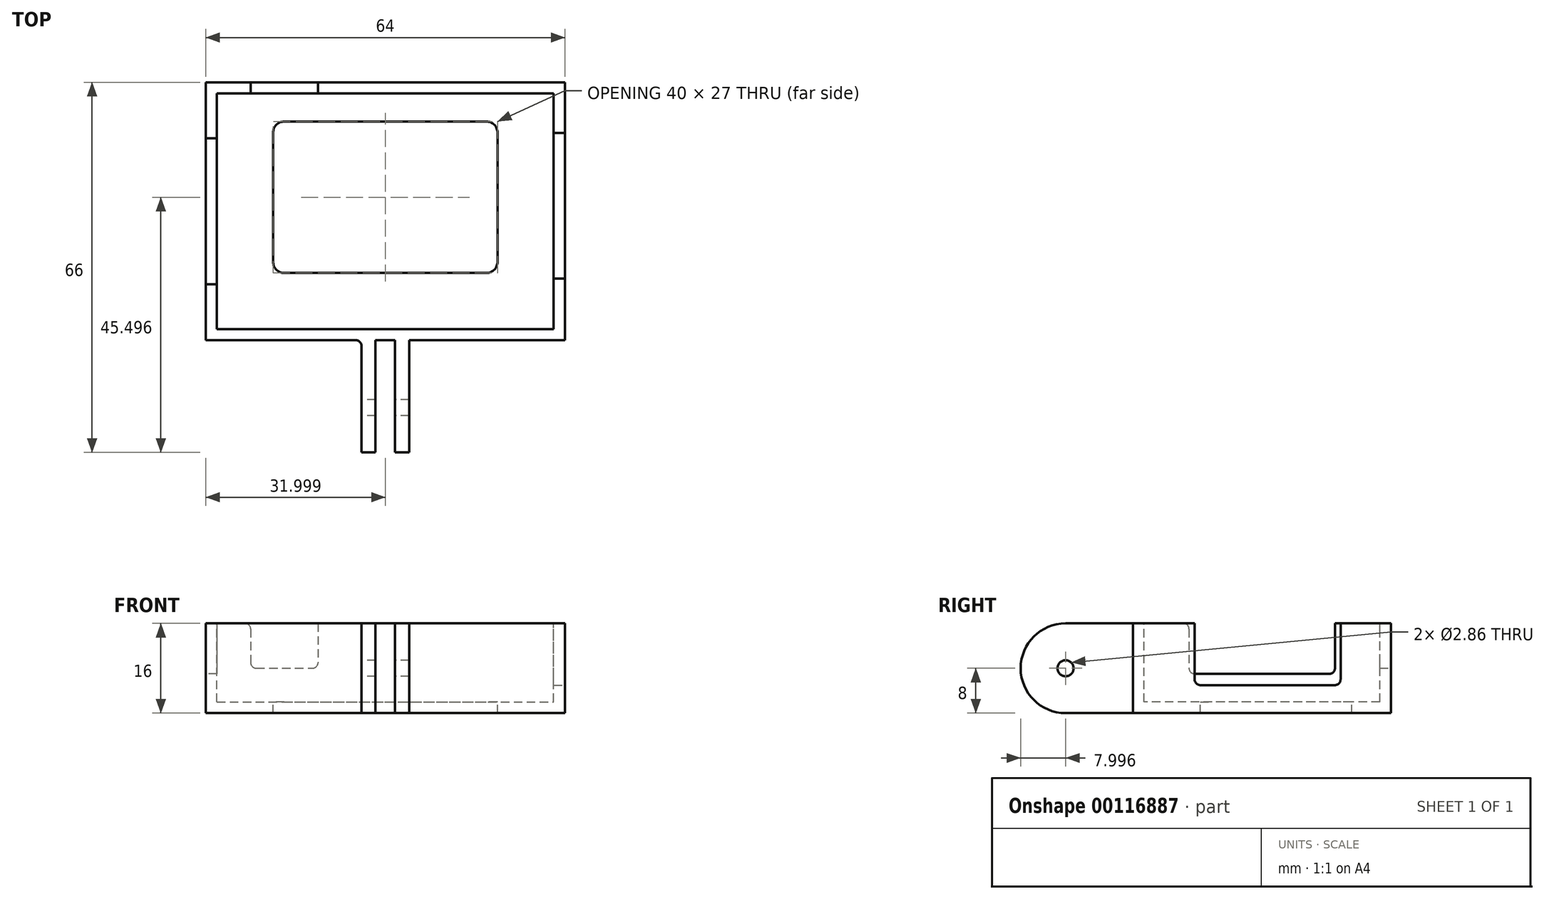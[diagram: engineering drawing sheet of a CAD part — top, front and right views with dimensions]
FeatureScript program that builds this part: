
annotation { "Feature Type Name" : "Feature", "Feature Type Description" : "" }
export const myFeature = defineFeature(function(context is Context, id is Id, definition is map)
    precondition{}
    {
        {
            var Q0;
            Q0=qCreatedBy(makeId("Top.planeOp"),FACE);
            var sketch = newSketch(context, id + "F0", { "sketchPlane" : qUnion([Q0])});
            skLineSegment(sketch, "E0.bottom", {"start": v(-24.87, 23.52) * mm, "end": v(39.13, 23.52) * mm});
            skLineSegment(sketch, "E0.top", {"start": v(-24.87, -22.48) * mm, "end": v(39.13, -22.48) * mm});
            skLineSegment(sketch, "E0.left", {"start": v(-24.87, 23.52) * mm, "end": v(-24.87, -22.48) * mm});
            skLineSegment(sketch, "E0.right", {"start": v(39.13, 23.52) * mm, "end": v(39.13, -22.48) * mm});
            skSolve(sketch);
        }
        {
            var Q0;
            Q0=makeQuery(id+"F0.imprint","IMPRINT",FACE,{"disambiguationData":[TD([[makeQuery(id+"F0.imprint","IMPRINT",EDGE,{"derivedFrom":sQuery(id+"F0.wireOp",EDGE,"E0.bottom")}),-1.0]])]});
            extrude(context, id + "F1", {"entities" : qUnion([Q0]), "depth" : 16 * mm});
        }
        {
            var Q0;
            Q0=makeQuery(id+"F1.opExtrude","CAP_FACE",FACE,{"disambiguationData":[OSD([sQuery(id+"F0.wireOp",EDGE,"E0.bottom"),sQuery(id+"F0.wireOp",EDGE,"E0.top"),sQuery(id+"F0.wireOp",EDGE,"E0.left"),sQuery(id+"F0.wireOp",EDGE,"E0.right")])],"isStart":false});
            var sketch = newSketch(context, id + "F2", { "sketchPlane" : qUnion([Q0])});
            skLineSegment(sketch, "E1.bottom", {"start": v(-22.87, 21.52) * mm, "end": v(37.13, 21.52) * mm});
            skLineSegment(sketch, "E1.top", {"start": v(-22.87, -20.48) * mm, "end": v(37.13, -20.48) * mm});
            skLineSegment(sketch, "E1.left", {"start": v(-22.87, 21.52) * mm, "end": v(-22.87, -20.48) * mm});
            skLineSegment(sketch, "E1.right", {"start": v(37.13, 21.52) * mm, "end": v(37.13, -20.48) * mm});
            skSolve(sketch);
        }
        {
            var Q0;
            Q0=makeQuery(id+"F2.imprint","IMPRINT",FACE,{"disambiguationData":[TD([[makeQuery(id+"F2.imprint","IMPRINT",EDGE,{"derivedFrom":sQuery(id+"F2.wireOp",EDGE,"E1.bottom")}),-1.0]])]});
            extrude(context, id + "F3", {"entities" : qUnion([Q0]), "operationType" : NewBodyOperationType.REMOVE, "oppositeDirection" : true, "depth" : 14 * mm});
        }
        {
            var Q0;
            Q0=makeQuery(id+"F3.boolean.opBoolean","COPY",FACE,{"derivedFrom":makeQuery(id+"F3.opExtrude","CAP_FACE",FACE,{"disambiguationData":[OSD([sQuery(id+"F2.wireOp",EDGE,"E1.bottom"),sQuery(id+"F2.wireOp",EDGE,"E1.top"),sQuery(id+"F2.wireOp",EDGE,"E1.left"),sQuery(id+"F2.wireOp",EDGE,"E1.right")])],"isStart":false})});
            var sketch = newSketch(context, id + "F4", { "sketchPlane" : qUnion([Q0])});
            skLineSegment(sketch, "E2.bottom", {"start": v(-12.87, 16.52) * mm, "end": v(27.13, 16.52) * mm});
            skLineSegment(sketch, "E2.top", {"start": v(-12.87, -10.48) * mm, "end": v(27.13, -10.48) * mm});
            skLineSegment(sketch, "E2.left", {"start": v(-12.87, 16.52) * mm, "end": v(-12.87, -10.48) * mm});
            skLineSegment(sketch, "E2.right", {"start": v(27.13, 16.52) * mm, "end": v(27.13, -10.48) * mm});
            skSolve(sketch);
        }
        {
            var Q0;
            Q0=makeQuery(id+"F4.imprint","IMPRINT",FACE,{"disambiguationData":[TD([[makeQuery(id+"F4.imprint","IMPRINT",EDGE,{"derivedFrom":sQuery(id+"F4.wireOp",EDGE,"E2.bottom")}),-1.0]])]});
            extrude(context, id + "F5", {"entities" : qUnion([Q0]), "operationType" : NewBodyOperationType.REMOVE, "oppositeDirection" : true, "depth" : 25 * mm});
        }
        {
            var Q0;
            Q0=makeQuery(id+"F5.boolean.opBoolean","COPY",EDGE,{"derivedFrom":makeQuery(id+"F5.opExtrude","SWEPT_EDGE",EDGE,{"disambiguationData":[OSD([sQuery(id+"F4.wireOp",EDGE,"E2.bottom"),sQuery(id+"F4.wireOp",EDGE,"E2.left")])]})});
            var Q1;
            Q1=makeQuery(id+"F5.boolean.opBoolean","COPY",EDGE,{"derivedFrom":makeQuery(id+"F5.opExtrude","SWEPT_EDGE",EDGE,{"disambiguationData":[OSD([sQuery(id+"F4.wireOp",EDGE,"E2.top"),sQuery(id+"F4.wireOp",EDGE,"E2.left")])]})});
            var Q2;
            Q2=makeQuery(id+"F5.boolean.opBoolean","COPY",EDGE,{"derivedFrom":makeQuery(id+"F5.opExtrude","SWEPT_EDGE",EDGE,{"disambiguationData":[OSD([sQuery(id+"F4.wireOp",EDGE,"E2.top"),sQuery(id+"F4.wireOp",EDGE,"E2.right")])]})});
            var Q3;
            Q3=makeQuery(id+"F5.boolean.opBoolean","COPY",EDGE,{"derivedFrom":makeQuery(id+"F5.opExtrude","SWEPT_EDGE",EDGE,{"disambiguationData":[OSD([sQuery(id+"F4.wireOp",EDGE,"E2.bottom"),sQuery(id+"F4.wireOp",EDGE,"E2.right")])]})});
            fillet(context, id + "F6", {"entities" : qUnion([Q0, Q1, Q2, Q3]), "radius" : 2 * mm, "tangentPropagation" : true, "allowEdgeOverflow" : false});
        }
        {
            var Q0;
            Q0=makeQuery(id+"F1.opExtrude","SWEPT_FACE",FACE,{"disambiguationData":[OSD([sQuery(id+"F0.wireOp",EDGE,"E0.top")])]});
            var sketch = newSketch(context, id + "F7", { "sketchPlane" : qUnion([Q0])});
            skLineSegment(sketch, "E3.bottom", {"start": v(2.88, 16) * mm, "end": v(5.38, 16) * mm});
            skLineSegment(sketch, "E3.top", {"start": v(2.88, 0) * mm, "end": v(5.38, 0) * mm});
            skLineSegment(sketch, "E3.left", {"start": v(2.88, 16) * mm, "end": v(2.88, 0) * mm});
            skLineSegment(sketch, "E3.right", {"start": v(5.38, 16) * mm, "end": v(5.38, 0) * mm});
            skLineSegment(sketch, "E4.1.0.0", {"start": v(8.88, 16) * mm, "end": v(8.88, 0) * mm});
            skLineSegment(sketch, "E4.1.0.1", {"start": v(11.38, 16) * mm, "end": v(11.38, 0) * mm});
            skLineSegment(sketch, "E4.1.0.2", {"start": v(8.88, 16) * mm, "end": v(11.38, 16) * mm});
            skLineSegment(sketch, "E4.1.0.3", {"start": v(8.88, 0) * mm, "end": v(11.38, 0) * mm});
            skLineSegment(sketch, "E4.direction1", {"start": v(2.88, 0) * mm, "end": v(8.88, 0) * mm, "construction": true});
            skSolve(sketch);
        }
        {
            var Q0;
            Q0=makeQuery(id+"F7.imprint","IMPRINT",FACE,{"disambiguationData":[TD([[makeQuery(id+"F7.imprint","IMPRINT",EDGE,{"derivedFrom":sQuery(id+"F7.wireOp",EDGE,"E3.bottom")}),-1.0]])]});
            var Q1;
            Q1=makeQuery(id+"F7.imprint","IMPRINT",FACE,{"disambiguationData":[TD([[makeQuery(id+"F7.imprint","IMPRINT",EDGE,{"derivedFrom":sQuery(id+"F7.wireOp",EDGE,"E4.1.0.0")}),1.0]])]});
            extrude(context, id + "F8", {"entities" : qUnion([Q0, Q1]), "operationType" : NewBodyOperationType.ADD, "depth" : 20 * mm});
        }
        {
            var Q0;
            Q0=makeQuery(id+"F8.opExtrude","SWEPT_FACE",FACE,{"disambiguationData":[OSD([sQuery(id+"F7.wireOp",EDGE,"E3.left")])]});
            var sketch = newSketch(context, id + "F9", { "sketchPlane" : qUnion([Q0])});
            skLineSegment(sketch, "E5", {"start": v(42.48, 8) * mm, "end": v(22.48, 8) * mm, "construction": true});
            skCircle(sketch, "E6", {"center": v(34.48, 8) * mm, "radius": 1.43 * mm});
            skCircle(sketch, "E7", {"center": v(34.48, 8) * mm, "radius": 8 * mm});
            skSolve(sketch);
        }
        {
            var Q0;
            Q0=makeQuery(id+"F9.imprint","IMPRINT",FACE,{"disambiguationData":[TD([[makeQuery(id+"F9.imprint","IMPRINT",EDGE,{"derivedFrom":sQuery(id+"F9.wireOp",EDGE,"E6")}),1.0]])]});
            var Q1;
            {var subQ0=sQuery(id+"F9.wireOp",EDGE,"E7");var subQ1=sQuery(id+"F7.wireOp",EDGE,"E3.left");var subQ4=makeQuery(id+"F8.opExtrude","CAP_EDGE",EDGE,{"disambiguationData":[OSD([subQ1])],"isStart":false});var subQ5=makeQuery(id+"F9.imprint","INTERSECT",VERTEX,{"derivedFrom":[subQ4,subQ0]});Q1=makeQuery(id+"F9.imprint","IMPRINT",FACE,{"disambiguationData":[TD([[makeQuery(id+"F9.imprint","IMPRINT",EDGE,{"disambiguationData":[TD([[subQ5,-1.0]])],"derivedFrom":subQ0}),-1.0]])]});}
            var Q2;
            {var subQ0=sQuery(id+"F9.wireOp",EDGE,"E7");var subQ1=sQuery(id+"F7.wireOp",EDGE,"E3.left");var subQ2=makeQuery(id+"F8.opExtrude","CAP_EDGE",EDGE,{"disambiguationData":[OSD([subQ1])],"isStart":false});var subQ3=makeQuery(id+"F9.imprint","INTERSECT",VERTEX,{"derivedFrom":[subQ2,subQ0]});Q2=makeQuery(id+"F9.imprint","IMPRINT",FACE,{"disambiguationData":[TD([[makeQuery(id+"F9.imprint","IMPRINT",EDGE,{"disambiguationData":[TD([[subQ3,1.0]])],"derivedFrom":subQ0}),-1.0]])]});}
            extrude(context, id + "F10", {"entities" : qUnion([Q0, Q1, Q2]), "operationType" : NewBodyOperationType.REMOVE, "oppositeDirection" : true, "depth" : 25 * mm});
        }
        {
            var Q0;
            Q0=makeQuery(id+"F1.opExtrude","SWEPT_FACE",FACE,{"disambiguationData":[OSD([sQuery(id+"F0.wireOp",EDGE,"E0.right")])]});
            var sketch = newSketch(context, id + "F11", { "sketchPlane" : qUnion([Q0])});
            skLineSegment(sketch, "E8.bottom", {"start": v(-11.48, 17.32) * mm, "end": v(14.52, 17.32) * mm});
            skLineSegment(sketch, "E8.top", {"start": v(-11.48, 5) * mm, "end": v(14.52, 5) * mm});
            skLineSegment(sketch, "E8.left", {"start": v(-11.48, 17.32) * mm, "end": v(-11.48, 5) * mm});
            skLineSegment(sketch, "E8.right", {"start": v(14.52, 17.32) * mm, "end": v(14.52, 5) * mm});
            skSolve(sketch);
        }
        {
            var Q0;
            {var subQ0=sQuery(id+"F11.wireOp",EDGE,"E8.top");Q0=makeQuery(id+"F11.imprint","IMPRINT",FACE,{"disambiguationData":[TD([[makeQuery(id+"F11.imprint","IMPRINT",EDGE,{"derivedFrom":subQ0}),1.0]])]});}
            extrude(context, id + "F12", {"entities" : qUnion([Q0]), "operationType" : NewBodyOperationType.REMOVE, "oppositeDirection" : true, "depth" : 25 * mm});
        }
        {
            var Q0;
            Q0=makeQuery(id+"F1.opExtrude","SWEPT_FACE",FACE,{"disambiguationData":[OSD([sQuery(id+"F0.wireOp",EDGE,"E0.left")])]});
            var sketch = newSketch(context, id + "F13", { "sketchPlane" : qUnion([Q0])});
            skLineSegment(sketch, "E9.bottom", {"start": v(-13.52, 18.92) * mm, "end": v(12.48, 18.92) * mm});
            skLineSegment(sketch, "E9.top", {"start": v(-13.52, 7) * mm, "end": v(12.48, 7) * mm});
            skLineSegment(sketch, "E9.left", {"start": v(-13.52, 18.92) * mm, "end": v(-13.52, 7) * mm});
            skLineSegment(sketch, "E9.right", {"start": v(12.48, 18.92) * mm, "end": v(12.48, 7) * mm});
            skSolve(sketch);
        }
        {
            var Q0;
            {var subQ0=sQuery(id+"F13.wireOp",EDGE,"E9.top");Q0=makeQuery(id+"F13.imprint","IMPRINT",FACE,{"disambiguationData":[TD([[makeQuery(id+"F13.imprint","IMPRINT",EDGE,{"derivedFrom":subQ0}),1.0]])]});}
            extrude(context, id + "F14", {"entities" : qUnion([Q0]), "operationType" : NewBodyOperationType.REMOVE, "oppositeDirection" : true, "depth" : 25 * mm});
        }
        {
            var Q0;
            Q0=makeQuery(id+"F1.opExtrude","SWEPT_FACE",FACE,{"disambiguationData":[OSD([sQuery(id+"F0.wireOp",EDGE,"E0.bottom")])]});
            var sketch = newSketch(context, id + "F15", { "sketchPlane" : qUnion([Q0])});
            skLineSegment(sketch, "E10.bottom", {"start": v(16.87, 16) * mm, "end": v(4.87, 16) * mm});
            skLineSegment(sketch, "E10.top", {"start": v(16.87, 8) * mm, "end": v(4.87, 8) * mm});
            skLineSegment(sketch, "E10.left", {"start": v(16.87, 16) * mm, "end": v(16.87, 8) * mm});
            skLineSegment(sketch, "E10.right", {"start": v(4.87, 16) * mm, "end": v(4.87, 8) * mm});
            skSolve(sketch);
        }
        {
            var Q0;
            Q0=makeQuery(id+"F15.imprint","IMPRINT",FACE,{"disambiguationData":[TD([[makeQuery(id+"F15.imprint","IMPRINT",EDGE,{"derivedFrom":sQuery(id+"F15.wireOp",EDGE,"E10.bottom")}),1.0]])]});
            extrude(context, id + "F16", {"entities" : qUnion([Q0]), "operationType" : NewBodyOperationType.REMOVE, "oppositeDirection" : true, "depth" : 25 * mm});
        }
        {
            var Q0;
            Q0=makeQuery(id+"F14.boolean.opBoolean","COPY",EDGE,{"derivedFrom":makeQuery(id+"F14.opExtrude","SWEPT_EDGE",EDGE,{"disambiguationData":[OSD([sQuery(id+"F0.wireOp",EDGE,"E0.left"),sQuery(id+"F13.wireOp",EDGE,"E9.left")])]})});
            var Q1;
            Q1=makeQuery(id+"F14.boolean.opBoolean","COPY",EDGE,{"derivedFrom":makeQuery(id+"F14.opExtrude","SWEPT_EDGE",EDGE,{"disambiguationData":[OSD([sQuery(id+"F0.wireOp",EDGE,"E0.left"),sQuery(id+"F13.wireOp",EDGE,"E9.right")])]})});
            var Q2;
            Q2=makeQuery(id+"F12.boolean.opBoolean","COPY",EDGE,{"derivedFrom":makeQuery(id+"F12.opExtrude","SWEPT_EDGE",EDGE,{"disambiguationData":[OSD([sQuery(id+"F0.wireOp",EDGE,"E0.right"),sQuery(id+"F11.wireOp",EDGE,"E8.right")])]})});
            var Q3;
            Q3=makeQuery(id+"F12.boolean.opBoolean","COPY",EDGE,{"derivedFrom":makeQuery(id+"F12.opExtrude","SWEPT_EDGE",EDGE,{"disambiguationData":[OSD([sQuery(id+"F0.wireOp",EDGE,"E0.right"),sQuery(id+"F11.wireOp",EDGE,"E8.left")])]})});
            var Q4;
            Q4=makeQuery(id+"F14.boolean.opBoolean","COPY",EDGE,{"derivedFrom":makeQuery(id+"F14.opExtrude","SWEPT_EDGE",EDGE,{"disambiguationData":[OSD([sQuery(id+"F13.wireOp",EDGE,"E9.top"),sQuery(id+"F13.wireOp",EDGE,"E9.left")])]})});
            var Q5;
            Q5=makeQuery(id+"F12.boolean.opBoolean","COPY",EDGE,{"derivedFrom":makeQuery(id+"F12.opExtrude","SWEPT_EDGE",EDGE,{"disambiguationData":[OSD([sQuery(id+"F11.wireOp",EDGE,"E8.top"),sQuery(id+"F11.wireOp",EDGE,"E8.right")])]})});
            var Q6;
            Q6=makeQuery(id+"F14.boolean.opBoolean","COPY",EDGE,{"derivedFrom":makeQuery(id+"F14.opExtrude","SWEPT_EDGE",EDGE,{"disambiguationData":[OSD([sQuery(id+"F13.wireOp",EDGE,"E9.top"),sQuery(id+"F13.wireOp",EDGE,"E9.right")])]})});
            var Q7;
            Q7=makeQuery(id+"F12.boolean.opBoolean","COPY",EDGE,{"derivedFrom":makeQuery(id+"F12.opExtrude","SWEPT_EDGE",EDGE,{"disambiguationData":[OSD([sQuery(id+"F11.wireOp",EDGE,"E8.top"),sQuery(id+"F11.wireOp",EDGE,"E8.left")])]})});
            var Q8;
            Q8=makeQuery(id+"F16.boolean.opBoolean","COPY",EDGE,{"derivedFrom":makeQuery(id+"F16.opExtrude","SWEPT_EDGE",EDGE,{"disambiguationData":[OSD([sQuery(id+"F0.wireOp",EDGE,"E0.bottom"),sQuery(id+"F15.wireOp",EDGE,"E10.bottom"),sQuery(id+"F15.wireOp",EDGE,"E10.right")])]})});
            var Q9;
            Q9=makeQuery(id+"F16.boolean.opBoolean","COPY",EDGE,{"derivedFrom":makeQuery(id+"F16.opExtrude","SWEPT_EDGE",EDGE,{"disambiguationData":[OSD([sQuery(id+"F0.wireOp",EDGE,"E0.bottom"),sQuery(id+"F15.wireOp",EDGE,"E10.bottom"),sQuery(id+"F15.wireOp",EDGE,"E10.left")])]})});
            var Q10;
            Q10=makeQuery(id+"F16.boolean.opBoolean","COPY",EDGE,{"derivedFrom":makeQuery(id+"F16.opExtrude","SWEPT_EDGE",EDGE,{"disambiguationData":[OSD([sQuery(id+"F15.wireOp",EDGE,"E10.top"),sQuery(id+"F15.wireOp",EDGE,"E10.right")])]})});
            var Q11;
            Q11=makeQuery(id+"F16.boolean.opBoolean","COPY",EDGE,{"derivedFrom":makeQuery(id+"F16.opExtrude","SWEPT_EDGE",EDGE,{"disambiguationData":[OSD([sQuery(id+"F15.wireOp",EDGE,"E10.top"),sQuery(id+"F15.wireOp",EDGE,"E10.left")])]})});
            var Q12;
            Q12=makeQuery(id+"F8.opExtrude","CAP_EDGE",EDGE,{"disambiguationData":[OSD([sQuery(id+"F7.wireOp",EDGE,"E3.left")])],"isStart":true});
            var Q13;
            Q13=makeQuery(id+"F8.opExtrude","CAP_EDGE",EDGE,{"disambiguationData":[OSD([sQuery(id+"F7.wireOp",EDGE,"E4.1.0.1")])],"isStart":true});
            fillet(context, id + "F17", {"entities" : qUnion([Q0, Q1, Q2, Q3, Q4, Q5, Q6, Q7, Q8, Q9, Q10, Q11, Q12, Q13]), "radius" : 1 * mm, "tangentPropagation" : true, "allowEdgeOverflow" : false});
        }
    });
